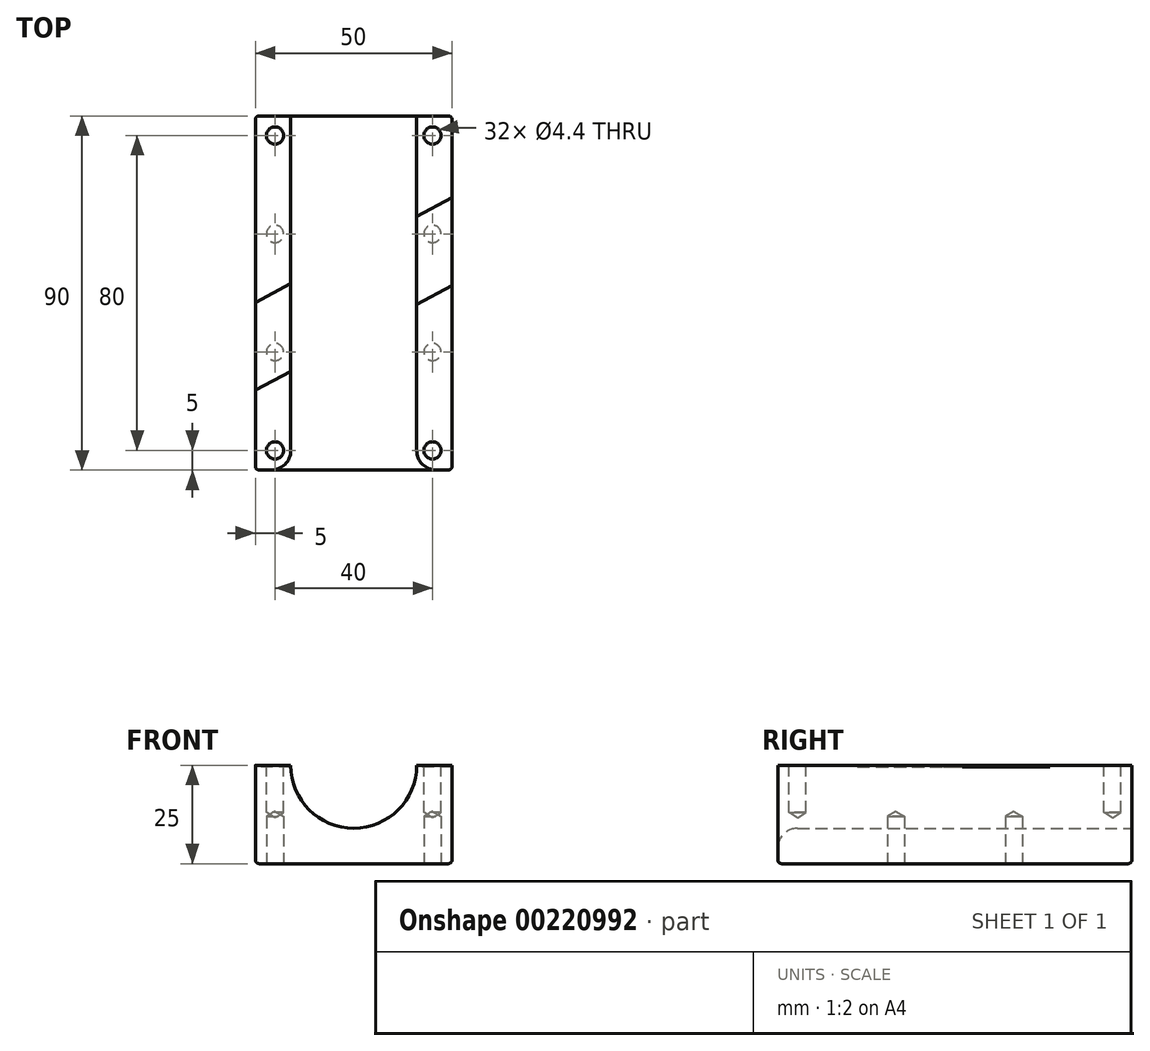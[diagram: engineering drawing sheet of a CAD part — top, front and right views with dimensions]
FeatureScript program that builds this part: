
annotation { "Feature Type Name" : "Feature", "Feature Type Description" : "" }
export const myFeature = defineFeature(function(context is Context, id is Id, definition is map)
    precondition{}
    {
        {
            var Q0;
            Q0=qCreatedBy(makeId("Front.planeOp"),FACE);
            var sketch = newSketch(context, id + "F0", { "sketchPlane" : qUnion([Q0])});
            skLineSegment(sketch, "E0.bottom", {"start": v(25, -25) * mm, "end": v(-25, -25) * mm});
            skLineSegment(sketch, "E0.left", {"start": v(25, -25) * mm, "end": v(25, 0) * mm});
            skLineSegment(sketch, "E0.right", {"start": v(-25, -25) * mm, "end": v(-25, 0) * mm});
            skPoint(sketch, "E0.middle", {"position": v(0, 0) * mm});
            skArc(sketch, "E1", {"start": v(-16, 0) * mm, "mid": v(0, -16) * mm, "end": v(16, 0) * mm});
            skLineSegment(sketch, "E2", {"start": v(-25, 0) * mm, "end": v(-16, 0) * mm});
            skLineSegment(sketch, "E3", {"start": v(16, 0) * mm, "end": v(25, 0) * mm});
            skPoint(sketch, "E4.orphan", {"position": v(-25, 25) * mm});
            skPoint(sketch, "E5.orphan", {"position": v(25, 25) * mm});
            skSolve(sketch);
        }
        {
            var Q0;
            Q0=makeQuery(id+"F0.imprint","IMPRINT",FACE,{"disambiguationData":[TD([[makeQuery(id+"F0.imprint","IMPRINT",EDGE,{"derivedFrom":sQuery(id+"F0.wireOp",EDGE,"E0.bottom")}),-1.0]])]});
            extrude(context, id + "F1", {"entities" : qUnion([Q0]), "depth" : 90 * mm});
        }
        {
            var Q0;
            Q0=makeQuery(id+"F1.opExtrude","SWEPT_FACE",FACE,{"disambiguationData":[OSD([sQuery(id+"F0.wireOp",EDGE,"E2")])]});
            var sketch = newSketch(context, id + "F2", { "sketchPlane" : qUnion([Q0])});
            skPoint(sketch, "E6", {"position": v(-20, -5) * mm});
            skPoint(sketch, "E7", {"position": v(20, -5) * mm});
            skPoint(sketch, "E8", {"position": v(20, -85) * mm});
            skPoint(sketch, "E9", {"position": v(-20, -85) * mm});
            skSolve(sketch);
        }
        {
            var Q0;
            Q0=sQuery(id+"F2.wireOp",VERTEX,"E6");
            var Q1;
            Q1=sQuery(id+"F2.wireOp",VERTEX,"E7");
            var Q2;
            Q2=sQuery(id+"F2.wireOp",VERTEX,"E8");
            var Q3;
            Q3=sQuery(id+"F2.wireOp",VERTEX,"E9");
            var Q4;
            Q4=makeQuery(id+"F1.opExtrude","SWEPT_BODY",BODY,{"disambiguationData":[OSD([sQuery(id+"F0.wireOp",EDGE,"E0.bottom"),sQuery(id+"F0.wireOp",EDGE,"E0.left"),sQuery(id+"F0.wireOp",EDGE,"E0.right"),sQuery(id+"F0.wireOp",EDGE,"E1"),sQuery(id+"F0.wireOp",EDGE,"E2"),sQuery(id+"F0.wireOp",EDGE,"E3")])]});
            hole(context, id + "F3", {"style" : HoleStyle.SIMPLE, "endStyle" : HoleEndStyle.BLIND, "standardTappedOrClearance" : lookupTablePath({ "standard" : "ISO", "fit" : "Normal", "size" : "M4", "type" : "Clearance" }), "standardBlindInLast" : lookupTablePath({ "fit" : "Standard", "standard" : "ISO", "size" : "M4", "type" : "Clearance" }), "holeDiameter" : 4.4 * mm, "holeDepth" : 12 * mm, "startFromSketch" : true, "locations" : qUnion([Q0, Q1, Q2, Q3]), "scope" : qUnion([Q4])});
        }
        {
            var Q0;
            Q0=makeQuery(id+"F1.opExtrude","CAP_EDGE",EDGE,{"disambiguationData":[OSD([sQuery(id+"F0.wireOp",EDGE,"E1")])],"isStart":false});
            fillet(context, id + "F4", {"entities" : qUnion([Q0]), "radius" : 5 * mm, "tangentPropagation" : true, "allowEdgeOverflow" : false});
        }
        {
            var Q0;
            Q0=makeQuery(id+"F1.opExtrude","SWEPT_FACE",FACE,{"disambiguationData":[OSD([sQuery(id+"F0.wireOp",EDGE,"E2")])]});
            var sketch = newSketch(context, id + "F5", { "sketchPlane" : qUnion([Q0])});
            skLineSegment(sketch, "E10", {"start": v(-25, -69.7) * mm, "end": v(31.27, -39.78) * mm});
            skLineSegment(sketch, "E11", {"start": v(31.27, -39.78) * mm, "end": v(31.27, -17.48) * mm});
            skLineSegment(sketch, "E12", {"start": v(31.27, -17.48) * mm, "end": v(-25, -47.4) * mm});
            skLineSegment(sketch, "E13", {"start": v(-25, -47.4) * mm, "end": v(-25, -69.7) * mm});
            skSolve(sketch);
        }
        {
            var Q0;
            {var subQ0=sQuery(id+"F5.wireOp",EDGE,"E11");Q0=makeQuery(id+"F5.imprint","IMPRINT",FACE,{"disambiguationData":[TD([[makeQuery(id+"F5.imprint","IMPRINT",EDGE,{"derivedFrom":subQ0}),1.0]])]});}
            var Q1;
            {var subQ0=sQuery(id+"F5.wireOp",EDGE,"E13");Q1=makeQuery(id+"F5.imprint","IMPRINT",FACE,{"disambiguationData":[TD([[makeQuery(id+"F5.imprint","IMPRINT",EDGE,{"derivedFrom":subQ0}),-1.0]])]});}
            extrude(context, id + "F6", {"entities" : qUnion([Q0, Q1]), "operationType" : NewBodyOperationType.REMOVE, "oppositeDirection" : true, "depth" : 0.46 * mm});
        }
        {
            var Q0;
            Q0=makeQuery(id+"F1.opExtrude","CAP_EDGE",EDGE,{"disambiguationData":[OSD([sQuery(id+"F0.wireOp",EDGE,"E0.left")])],"isStart":false});
            var Q1;
            Q1=makeQuery(id+"F1.opExtrude","SWEPT_EDGE",EDGE,{"disambiguationData":[OSD([sQuery(id+"F0.wireOp",EDGE,"E0.bottom"),sQuery(id+"F0.wireOp",EDGE,"E0.left")])]});
            var Q2;
            Q2=makeQuery(id+"F1.opExtrude","CAP_EDGE",EDGE,{"disambiguationData":[OSD([sQuery(id+"F0.wireOp",EDGE,"E0.left")])],"isStart":true});
            var Q3;
            Q3=makeQuery(id+"F1.opExtrude","CAP_EDGE",EDGE,{"disambiguationData":[OSD([sQuery(id+"F0.wireOp",EDGE,"E0.bottom")])],"isStart":false});
            var Q4;
            Q4=makeQuery(id+"F1.opExtrude","CAP_EDGE",EDGE,{"disambiguationData":[OSD([sQuery(id+"F0.wireOp",EDGE,"E0.right")])],"isStart":false});
            var Q5;
            Q5=makeQuery(id+"F1.opExtrude","CAP_EDGE",EDGE,{"disambiguationData":[OSD([sQuery(id+"F0.wireOp",EDGE,"E0.bottom")])],"isStart":true});
            var Q6;
            Q6=makeQuery(id+"F1.opExtrude","CAP_EDGE",EDGE,{"disambiguationData":[OSD([sQuery(id+"F0.wireOp",EDGE,"E0.right")])],"isStart":true});
            var Q7;
            Q7=makeQuery(id+"F1.opExtrude","SWEPT_EDGE",EDGE,{"disambiguationData":[OSD([sQuery(id+"F0.wireOp",EDGE,"E0.bottom"),sQuery(id+"F0.wireOp",EDGE,"E0.right")])]});
            fillet(context, id + "F7", {"entities" : qUnion([Q0, Q1, Q2, Q3, Q4, Q5, Q6, Q7]), "radius" : 1 * mm, "tangentPropagation" : true, "allowEdgeOverflow" : false});
        }
        {
            var Q0;
            Q0=makeQuery(id+"F1.opExtrude","SWEPT_FACE",FACE,{"disambiguationData":[OSD([sQuery(id+"F0.wireOp",EDGE,"E0.bottom")])]});
            var sketch = newSketch(context, id + "F8", { "sketchPlane" : qUnion([Q0])});
            skPoint(sketch, "E14", {"position": v(-20, 60) * mm});
            skPoint(sketch, "E15", {"position": v(20, 60) * mm});
            skPoint(sketch, "E16", {"position": v(20, 30) * mm});
            skPoint(sketch, "E17", {"position": v(-20, 30) * mm});
            skSolve(sketch);
        }
        {
            var Q0;
            Q0=sQuery(id+"F8.wireOp",VERTEX,"E16");
            var Q1;
            Q1=sQuery(id+"F8.wireOp",VERTEX,"E17");
            var Q2;
            Q2=sQuery(id+"F8.wireOp",VERTEX,"E14");
            var Q3;
            Q3=sQuery(id+"F8.wireOp",VERTEX,"E15");
            var Q4;
            Q4=makeQuery(id+"F1.opExtrude","SWEPT_BODY",BODY,{"disambiguationData":[OSD([sQuery(id+"F0.wireOp",EDGE,"E0.bottom"),sQuery(id+"F0.wireOp",EDGE,"E0.left"),sQuery(id+"F0.wireOp",EDGE,"E0.right"),sQuery(id+"F0.wireOp",EDGE,"E1"),sQuery(id+"F0.wireOp",EDGE,"E2"),sQuery(id+"F0.wireOp",EDGE,"E3")])]});
            hole(context, id + "F9", {"style" : HoleStyle.SIMPLE, "endStyle" : HoleEndStyle.BLIND, "standardTappedOrClearance" : lookupTablePath({ "standard" : "ISO", "fit" : "Normal", "size" : "M4", "type" : "Clearance" }), "standardBlindInLast" : lookupTablePath({ "fit" : "Standard", "standard" : "ISO", "size" : "M4", "type" : "Clearance" }), "holeDiameter" : 4.4 * mm, "holeDepth" : 12 * mm, "startFromSketch" : true, "locations" : qUnion([Q0, Q1, Q2, Q3]), "scope" : qUnion([Q4])});
        }
    });
